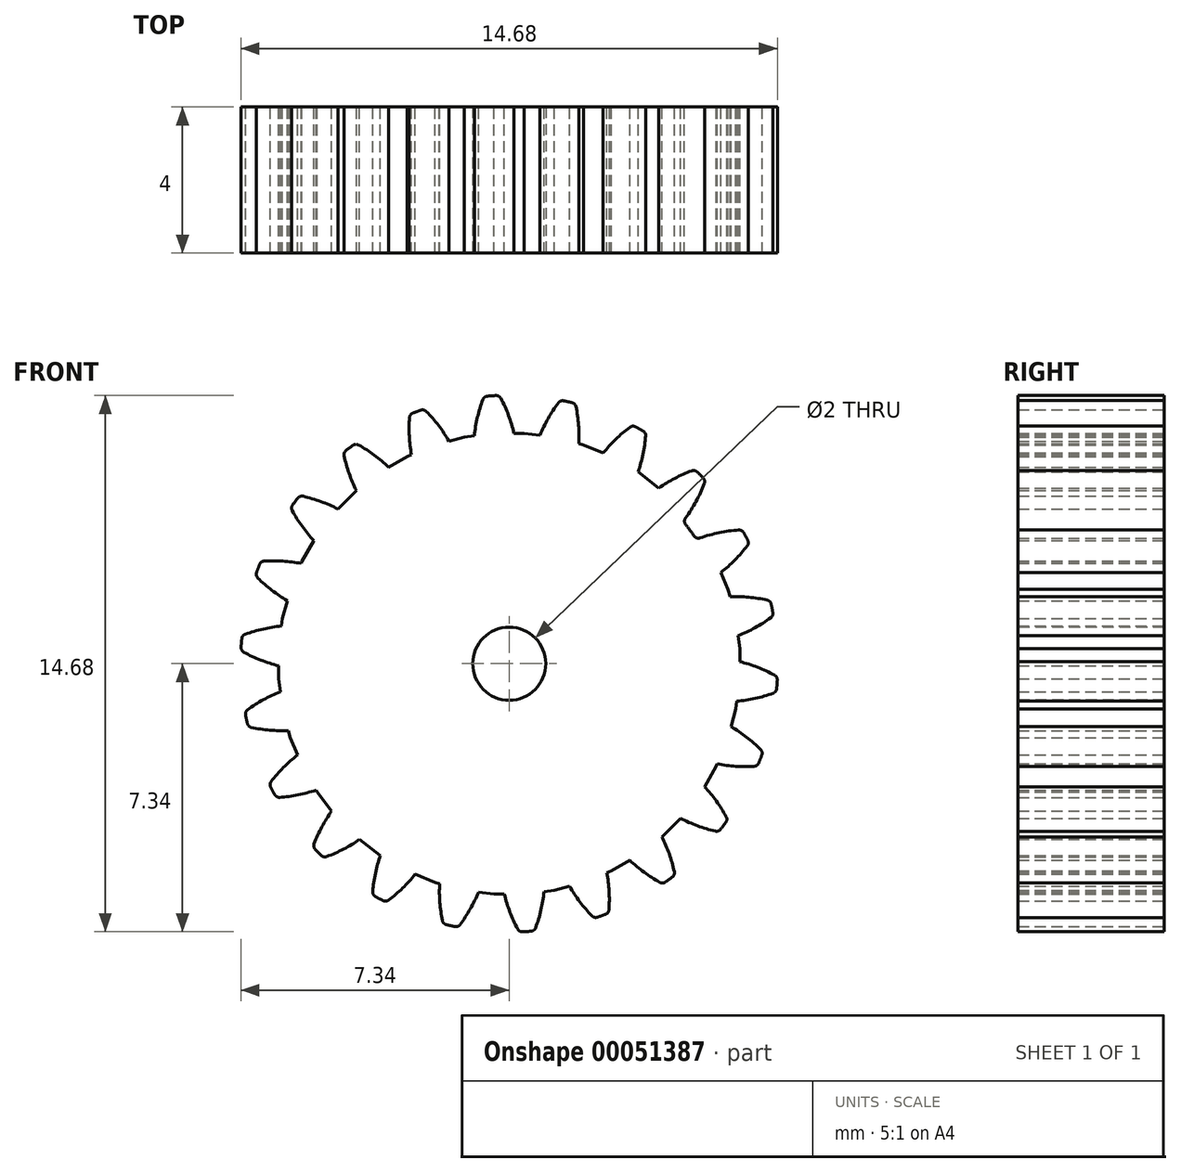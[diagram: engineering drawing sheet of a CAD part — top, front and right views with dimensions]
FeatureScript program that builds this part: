
annotation { "Feature Type Name" : "Feature", "Feature Type Description" : "" }
export const myFeature = defineFeature(function(context is Context, id is Id, definition is map)
    precondition{}
    {
        {
            var Q0;
            Q0=qCreatedBy(makeId("Front.planeOp"),FACE);
            var sketch = newSketch(context, id + "F0", { "sketchPlane" : qUnion([Q0])});
            skCircle(sketch, "E0", {"center": v(0, 0) * mm, "radius": 6.15 * mm, "construction": true});
            skCircle(sketch, "E1", {"center": v(0, 0) * mm, "radius": 6.75 * mm, "construction": true});
            skCircle(sketch, "E2", {"center": v(0, 0) * mm, "radius": 7.35 * mm, "construction": true});
            skLineSegment(sketch, "E3", {"start": v(0, 0) * mm, "end": v(0, 6.31) * mm, "construction": true});
            skCircle(sketch, "E4", {"center": v(0, 6.75) * mm, "radius": 4.05 * mm, "construction": true});
            skCircle(sketch, "E5.cCircle", {"center": v(0, 0) * mm, "radius": 6.31 * mm, "construction": true});
            skLineSegment(sketch, "E5.0", {"start": v(0, 6.31) * mm, "end": v(0.82, 6.26) * mm, "construction": true});
            skLineSegment(sketch, "E5.1", {"start": v(0.82, 6.26) * mm, "end": v(1.63, 6.1) * mm, "construction": true});
            skLineSegment(sketch, "E5.2", {"start": v(1.63, 6.1) * mm, "end": v(2.41, 5.83) * mm, "construction": true});
            skLineSegment(sketch, "E5.3", {"start": v(2.41, 5.83) * mm, "end": v(3.16, 5.46) * mm, "construction": true});
            skLineSegment(sketch, "E5.4", {"start": v(3.16, 5.46) * mm, "end": v(3.84, 5) * mm, "construction": true});
            skLineSegment(sketch, "E5.5", {"start": v(3.84, 5) * mm, "end": v(4.46, 4.46) * mm, "construction": true});
            skLineSegment(sketch, "E5.6", {"start": v(4.46, 4.46) * mm, "end": v(5, 3.84) * mm, "construction": true});
            skLineSegment(sketch, "E5.7", {"start": v(5, 3.84) * mm, "end": v(5.46, 3.16) * mm, "construction": true});
            skLineSegment(sketch, "E5.8", {"start": v(5.46, 3.16) * mm, "end": v(5.83, 2.41) * mm, "construction": true});
            skLineSegment(sketch, "E5.9", {"start": v(5.83, 2.41) * mm, "end": v(6.1, 1.63) * mm, "construction": true});
            skLineSegment(sketch, "E5.10", {"start": v(6.1, 1.63) * mm, "end": v(6.26, 0.82) * mm, "construction": true});
            skLineSegment(sketch, "E5.11", {"start": v(6.26, 0.82) * mm, "end": v(6.31, 0) * mm, "construction": true});
            skLineSegment(sketch, "E5.12", {"start": v(6.31, 0) * mm, "end": v(6.26, -0.82) * mm, "construction": true});
            skLineSegment(sketch, "E5.13", {"start": v(6.26, -0.82) * mm, "end": v(6.1, -1.63) * mm, "construction": true});
            skLineSegment(sketch, "E5.14", {"start": v(6.1, -1.63) * mm, "end": v(5.83, -2.41) * mm, "construction": true});
            skLineSegment(sketch, "E5.15", {"start": v(5.83, -2.41) * mm, "end": v(5.46, -3.16) * mm, "construction": true});
            skLineSegment(sketch, "E5.16", {"start": v(5.46, -3.16) * mm, "end": v(5, -3.84) * mm, "construction": true});
            skLineSegment(sketch, "E5.17", {"start": v(5, -3.84) * mm, "end": v(4.46, -4.46) * mm, "construction": true});
            skLineSegment(sketch, "E5.18", {"start": v(4.46, -4.46) * mm, "end": v(3.84, -5) * mm, "construction": true});
            skLineSegment(sketch, "E5.19", {"start": v(3.84, -5) * mm, "end": v(3.16, -5.46) * mm, "construction": true});
            skLineSegment(sketch, "E5.20", {"start": v(3.16, -5.46) * mm, "end": v(2.41, -5.83) * mm, "construction": true});
            skLineSegment(sketch, "E5.21", {"start": v(2.41, -5.83) * mm, "end": v(1.63, -6.1) * mm, "construction": true});
            skLineSegment(sketch, "E5.22", {"start": v(1.63, -6.1) * mm, "end": v(0.82, -6.26) * mm, "construction": true});
            skLineSegment(sketch, "E5.23", {"start": v(0.82, -6.26) * mm, "end": v(0, -6.31) * mm, "construction": true});
            skLineSegment(sketch, "E5.24", {"start": v(0, -6.31) * mm, "end": v(-0.82, -6.26) * mm, "construction": true});
            skLineSegment(sketch, "E5.25", {"start": v(-0.82, -6.26) * mm, "end": v(-1.63, -6.1) * mm, "construction": true});
            skLineSegment(sketch, "E5.26", {"start": v(-1.63, -6.1) * mm, "end": v(-2.41, -5.83) * mm, "construction": true});
            skLineSegment(sketch, "E5.27", {"start": v(-2.41, -5.83) * mm, "end": v(-3.16, -5.46) * mm, "construction": true});
            skLineSegment(sketch, "E5.28", {"start": v(-3.16, -5.46) * mm, "end": v(-3.84, -5) * mm, "construction": true});
            skLineSegment(sketch, "E5.29", {"start": v(-3.84, -5) * mm, "end": v(-4.46, -4.46) * mm, "construction": true});
            skLineSegment(sketch, "E5.30", {"start": v(-4.46, -4.46) * mm, "end": v(-5, -3.84) * mm, "construction": true});
            skLineSegment(sketch, "E5.31", {"start": v(-5, -3.84) * mm, "end": v(-5.46, -3.16) * mm, "construction": true});
            skLineSegment(sketch, "E5.32", {"start": v(-5.46, -3.16) * mm, "end": v(-5.83, -2.41) * mm, "construction": true});
            skLineSegment(sketch, "E5.33", {"start": v(-5.83, -2.41) * mm, "end": v(-6.1, -1.63) * mm, "construction": true});
            skLineSegment(sketch, "E5.34", {"start": v(-6.1, -1.63) * mm, "end": v(-6.26, -0.82) * mm, "construction": true});
            skLineSegment(sketch, "E5.35", {"start": v(-6.26, -0.82) * mm, "end": v(-6.31, 0) * mm, "construction": true});
            skLineSegment(sketch, "E5.36", {"start": v(-6.31, 0) * mm, "end": v(-6.26, 0.82) * mm, "construction": true});
            skLineSegment(sketch, "E5.37", {"start": v(-6.26, 0.82) * mm, "end": v(-6.1, 1.63) * mm, "construction": true});
            skLineSegment(sketch, "E5.38", {"start": v(-6.1, 1.63) * mm, "end": v(-5.83, 2.41) * mm, "construction": true});
            skLineSegment(sketch, "E5.39", {"start": v(-5.83, 2.41) * mm, "end": v(-5.46, 3.16) * mm, "construction": true});
            skLineSegment(sketch, "E5.40", {"start": v(-5.46, 3.16) * mm, "end": v(-5, 3.84) * mm, "construction": true});
            skLineSegment(sketch, "E5.41", {"start": v(-5, 3.84) * mm, "end": v(-4.46, 4.46) * mm, "construction": true});
            skLineSegment(sketch, "E5.42", {"start": v(-4.46, 4.46) * mm, "end": v(-3.84, 5) * mm, "construction": true});
            skLineSegment(sketch, "E5.43", {"start": v(-3.84, 5) * mm, "end": v(-3.16, 5.46) * mm, "construction": true});
            skLineSegment(sketch, "E5.44", {"start": v(-3.16, 5.46) * mm, "end": v(-2.41, 5.83) * mm, "construction": true});
            skLineSegment(sketch, "E5.45", {"start": v(-2.41, 5.83) * mm, "end": v(-1.63, 6.1) * mm, "construction": true});
            skLineSegment(sketch, "E5.46", {"start": v(-1.63, 6.1) * mm, "end": v(-0.82, 6.26) * mm, "construction": true});
            skLineSegment(sketch, "E5.47", {"start": v(-0.82, 6.26) * mm, "end": v(0, 6.31) * mm, "construction": true});
            skLineSegment(sketch, "E6.0", {"start": v(-0.41, 6.31) * mm, "end": v(0.41, 6.31) * mm});
            skLineSegment(sketch, "E6.1", {"start": v(0.41, 6.31) * mm, "end": v(1.23, 6.2) * mm});
            skLineSegment(sketch, "E6.2", {"start": v(1.23, 6.2) * mm, "end": v(2.03, 5.99) * mm});
            skLineSegment(sketch, "E6.3", {"start": v(2.03, 5.99) * mm, "end": v(2.8, 5.67) * mm});
            skLineSegment(sketch, "E6.4", {"start": v(2.8, 5.67) * mm, "end": v(3.51, 5.26) * mm});
            skLineSegment(sketch, "E6.5", {"start": v(3.51, 5.26) * mm, "end": v(4.17, 4.75) * mm});
            skLineSegment(sketch, "E6.6", {"start": v(4.17, 4.75) * mm, "end": v(4.75, 4.17) * mm});
            skLineSegment(sketch, "E6.7", {"start": v(4.75, 4.17) * mm, "end": v(5.26, 3.51) * mm, "construction": true});
            skLineSegment(sketch, "E6.8", {"start": v(5.26, 3.51) * mm, "end": v(5.67, 2.8) * mm});
            skLineSegment(sketch, "E6.9", {"start": v(5.67, 2.8) * mm, "end": v(5.99, 2.03) * mm});
            skLineSegment(sketch, "E6.10", {"start": v(5.99, 2.03) * mm, "end": v(6.2, 1.23) * mm});
            skLineSegment(sketch, "E6.11", {"start": v(6.2, 1.23) * mm, "end": v(6.31, 0.41) * mm});
            skLineSegment(sketch, "E6.12", {"start": v(6.31, 0.41) * mm, "end": v(6.31, -0.41) * mm});
            skLineSegment(sketch, "E6.13", {"start": v(6.31, -0.41) * mm, "end": v(6.2, -1.23) * mm});
            skLineSegment(sketch, "E6.14", {"start": v(6.2, -1.23) * mm, "end": v(5.99, -2.03) * mm});
            skLineSegment(sketch, "E6.15", {"start": v(5.99, -2.03) * mm, "end": v(5.67, -2.8) * mm});
            skLineSegment(sketch, "E6.16", {"start": v(5.67, -2.8) * mm, "end": v(5.26, -3.51) * mm});
            skLineSegment(sketch, "E6.17", {"start": v(5.26, -3.51) * mm, "end": v(4.75, -4.17) * mm});
            skLineSegment(sketch, "E6.18", {"start": v(4.75, -4.17) * mm, "end": v(4.17, -4.75) * mm});
            skLineSegment(sketch, "E6.19", {"start": v(4.17, -4.75) * mm, "end": v(3.51, -5.26) * mm});
            skLineSegment(sketch, "E6.20", {"start": v(3.51, -5.26) * mm, "end": v(2.8, -5.67) * mm});
            skLineSegment(sketch, "E6.21", {"start": v(2.8, -5.67) * mm, "end": v(2.03, -5.99) * mm});
            skLineSegment(sketch, "E6.22", {"start": v(2.03, -5.99) * mm, "end": v(1.23, -6.2) * mm});
            skLineSegment(sketch, "E6.23", {"start": v(1.23, -6.2) * mm, "end": v(0.41, -6.31) * mm});
            skLineSegment(sketch, "E6.24", {"start": v(0.41, -6.31) * mm, "end": v(-0.41, -6.31) * mm});
            skLineSegment(sketch, "E6.25", {"start": v(-0.41, -6.31) * mm, "end": v(-1.23, -6.2) * mm});
            skLineSegment(sketch, "E6.26", {"start": v(-1.23, -6.2) * mm, "end": v(-2.03, -5.99) * mm});
            skLineSegment(sketch, "E6.27", {"start": v(-2.03, -5.99) * mm, "end": v(-2.8, -5.67) * mm});
            skLineSegment(sketch, "E6.28", {"start": v(-2.8, -5.67) * mm, "end": v(-3.51, -5.26) * mm});
            skLineSegment(sketch, "E6.29", {"start": v(-3.51, -5.26) * mm, "end": v(-4.17, -4.75) * mm});
            skLineSegment(sketch, "E6.30", {"start": v(-4.17, -4.75) * mm, "end": v(-4.75, -4.17) * mm});
            skLineSegment(sketch, "E6.31", {"start": v(-4.75, -4.17) * mm, "end": v(-5.26, -3.51) * mm});
            skLineSegment(sketch, "E6.32", {"start": v(-5.26, -3.51) * mm, "end": v(-5.67, -2.8) * mm});
            skLineSegment(sketch, "E6.33", {"start": v(-5.67, -2.8) * mm, "end": v(-5.99, -2.03) * mm});
            skLineSegment(sketch, "E6.34", {"start": v(-5.99, -2.03) * mm, "end": v(-6.2, -1.23) * mm});
            skLineSegment(sketch, "E6.35", {"start": v(-6.2, -1.23) * mm, "end": v(-6.31, -0.41) * mm});
            skLineSegment(sketch, "E6.36", {"start": v(-6.31, -0.41) * mm, "end": v(-6.31, 0.41) * mm});
            skLineSegment(sketch, "E6.37", {"start": v(-6.31, 0.41) * mm, "end": v(-6.2, 1.23) * mm});
            skLineSegment(sketch, "E6.38", {"start": v(-6.2, 1.23) * mm, "end": v(-5.99, 2.03) * mm});
            skLineSegment(sketch, "E6.39", {"start": v(-5.99, 2.03) * mm, "end": v(-5.67, 2.8) * mm});
            skLineSegment(sketch, "E6.40", {"start": v(-5.67, 2.8) * mm, "end": v(-5.26, 3.51) * mm});
            skLineSegment(sketch, "E6.41", {"start": v(-5.26, 3.51) * mm, "end": v(-4.75, 4.17) * mm});
            skLineSegment(sketch, "E6.42", {"start": v(-4.75, 4.17) * mm, "end": v(-4.17, 4.75) * mm});
            skLineSegment(sketch, "E6.43", {"start": v(-4.17, 4.75) * mm, "end": v(-3.51, 5.26) * mm});
            skLineSegment(sketch, "E6.44", {"start": v(-3.51, 5.26) * mm, "end": v(-2.8, 5.67) * mm});
            skLineSegment(sketch, "E6.45", {"start": v(-2.8, 5.67) * mm, "end": v(-2.03, 5.99) * mm});
            skLineSegment(sketch, "E6.46", {"start": v(-2.03, 5.99) * mm, "end": v(-1.23, 6.2) * mm});
            skLineSegment(sketch, "E6.47", {"start": v(-1.23, 6.2) * mm, "end": v(-0.41, 6.31) * mm});
            skPoint(sketch, "E6.0.midPoint", {"position": v(0, 6.31) * mm});
            skLineSegment(sketch, "E7", {"start": v(0, 6.75) * mm, "end": v(-9.03, 6.75) * mm, "construction": true});
            skLineSegment(sketch, "E8", {"start": v(0, 6.75) * mm, "end": v(-8.97, 3.48) * mm, "construction": true});
            skCircle(sketch, "E9", {"center": v(-3.8, 5.36) * mm, "radius": 4.05 * mm, "construction": true});
            skArc(sketch, "E10", {"start": v(-0.23, 7.26) * mm, "mid": v(0, 6.77) * mm, "end": v(0.15, 6.26) * mm});
            skLineSegment(sketch, "E11", {"start": v(0, 0) * mm, "end": v(-0.41, 6.31) * mm, "construction": true});
            skArc(sketch, "E12.MirrorCS", {"start": v(-0.72, 7.23) * mm, "mid": v(-0.88, 6.72) * mm, "end": v(-0.96, 6.18) * mm});
            skArc(sketch, "E13", {"start": v(-0.6, 7.33) * mm, "mid": v(-0.48, 7.33) * mm, "end": v(-0.36, 7.34) * mm});
            skArc(sketch, "E14", {"start": v(-1.08, 6.05) * mm, "mid": v(0.4, -6.14) * mm, "end": v(0.28, 6.14) * mm});
            skPoint(sketch, "E15.visualSharp", {"position": v(-0.97, 6.07) * mm});
            skArc(sketch, "E15.filletArc", {"start": v(-1.08, 6.05) * mm, "mid": v(-1, 6.1) * mm, "end": v(-0.96, 6.18) * mm});
            skPoint(sketch, "E16.visualSharp", {"position": v(0.17, 6.15) * mm});
            skArc(sketch, "E16.filletArc", {"start": v(0.15, 6.26) * mm, "mid": v(0.2, 6.18) * mm, "end": v(0.28, 6.14) * mm});
            skPoint(sketch, "E17.visualSharp", {"position": v(-0.69, 7.32) * mm});
            skArc(sketch, "E17.filletArc", {"start": v(-0.6, 7.33) * mm, "mid": v(-0.67, 7.3) * mm, "end": v(-0.72, 7.23) * mm});
            skPoint(sketch, "E18.visualSharp", {"position": v(-0.27, 7.34) * mm});
            skArc(sketch, "E18.filletArc", {"start": v(-0.23, 7.26) * mm, "mid": v(-0.29, 7.32) * mm, "end": v(-0.36, 7.34) * mm});
            skArc(sketch, "E19.1.0", {"start": v(-2.74, 5.5) * mm, "mid": v(-2.68, 5.57) * mm, "end": v(-2.66, 5.66) * mm});
            skArc(sketch, "E19.1.1", {"start": v(-2.73, 6.74) * mm, "mid": v(-2.73, 6.2) * mm, "end": v(-2.66, 5.66) * mm});
            skArc(sketch, "E19.1.2", {"start": v(-2.64, 6.86) * mm, "mid": v(-2.7, 6.81) * mm, "end": v(-2.73, 6.74) * mm});
            skArc(sketch, "E19.1.3", {"start": v(-2.64, 6.86) * mm, "mid": v(-2.53, 6.9) * mm, "end": v(-2.42, 6.94) * mm});
            skArc(sketch, "E19.1.4", {"start": v(-2.27, 6.9) * mm, "mid": v(-2.34, 6.95) * mm, "end": v(-2.42, 6.94) * mm});
            skArc(sketch, "E19.1.5", {"start": v(-2.27, 6.9) * mm, "mid": v(-1.92, 6.5) * mm, "end": v(-1.62, 6.04) * mm});
            skArc(sketch, "E19.1.6", {"start": v(-1.62, 6.04) * mm, "mid": v(-1.56, 5.98) * mm, "end": v(-1.46, 5.97) * mm});
            skArc(sketch, "E19.2.0", {"start": v(-4.18, 4.51) * mm, "mid": v(-4.14, 4.6) * mm, "end": v(-4.15, 4.68) * mm});
            skArc(sketch, "E19.2.1", {"start": v(-4.52, 5.7) * mm, "mid": v(-4.37, 5.18) * mm, "end": v(-4.15, 4.68) * mm});
            skArc(sketch, "E19.2.2", {"start": v(-4.46, 5.84) * mm, "mid": v(-4.51, 5.77) * mm, "end": v(-4.52, 5.7) * mm});
            skArc(sketch, "E19.2.3", {"start": v(-4.46, 5.84) * mm, "mid": v(-4.37, 5.91) * mm, "end": v(-4.27, 5.98) * mm});
            skArc(sketch, "E19.2.4", {"start": v(-4.12, 5.99) * mm, "mid": v(-4.2, 6) * mm, "end": v(-4.27, 5.98) * mm});
            skArc(sketch, "E19.2.5", {"start": v(-4.12, 5.99) * mm, "mid": v(-3.67, 5.7) * mm, "end": v(-3.26, 5.34) * mm});
            skArc(sketch, "E19.2.6", {"start": v(-3.26, 5.34) * mm, "mid": v(-3.18, 5.3) * mm, "end": v(-3.09, 5.32) * mm});
            skArc(sketch, "E19.3.0", {"start": v(-5.28, 3.15) * mm, "mid": v(-5.26, 3.24) * mm, "end": v(-5.3, 3.32) * mm});
            skArc(sketch, "E19.3.1", {"start": v(-5.94, 4.2) * mm, "mid": v(-5.65, 3.74) * mm, "end": v(-5.3, 3.32) * mm});
            skArc(sketch, "E19.3.2", {"start": v(-5.93, 4.35) * mm, "mid": v(-5.96, 4.27) * mm, "end": v(-5.94, 4.2) * mm});
            skArc(sketch, "E19.3.3", {"start": v(-5.93, 4.35) * mm, "mid": v(-5.86, 4.44) * mm, "end": v(-5.79, 4.53) * mm});
            skArc(sketch, "E19.3.4", {"start": v(-5.64, 4.58) * mm, "mid": v(-5.72, 4.58) * mm, "end": v(-5.79, 4.53) * mm});
            skArc(sketch, "E19.3.5", {"start": v(-5.64, 4.58) * mm, "mid": v(-5.12, 4.43) * mm, "end": v(-4.63, 4.2) * mm});
            skArc(sketch, "E19.3.6", {"start": v(-4.63, 4.2) * mm, "mid": v(-4.54, 4.2) * mm, "end": v(-4.46, 4.23) * mm});
            skArc(sketch, "E19.4.0", {"start": v(-5.96, 1.53) * mm, "mid": v(-5.96, 1.63) * mm, "end": v(-6.02, 1.7) * mm});
            skArc(sketch, "E19.4.1", {"start": v(-6.88, 2.35) * mm, "mid": v(-6.47, 2) * mm, "end": v(-6.02, 1.7) * mm});
            skArc(sketch, "E19.4.2", {"start": v(-6.91, 2.5) * mm, "mid": v(-6.92, 2.42) * mm, "end": v(-6.88, 2.35) * mm});
            skArc(sketch, "E19.4.3", {"start": v(-6.91, 2.5) * mm, "mid": v(-6.87, 2.6) * mm, "end": v(-6.83, 2.72) * mm});
            skArc(sketch, "E19.4.4", {"start": v(-6.7, 2.8) * mm, "mid": v(-6.78, 2.78) * mm, "end": v(-6.83, 2.72) * mm});
            skArc(sketch, "E19.4.5", {"start": v(-6.7, 2.8) * mm, "mid": v(-6.16, 2.8) * mm, "end": v(-5.63, 2.73) * mm});
            skArc(sketch, "E19.4.6", {"start": v(-5.63, 2.73) * mm, "mid": v(-5.54, 2.74) * mm, "end": v(-5.47, 2.8) * mm});
            skArc(sketch, "E19.5.0", {"start": v(-6.15, -0.2) * mm, "mid": v(-6.18, -0.12) * mm, "end": v(-6.26, -0.07) * mm});
            skArc(sketch, "E19.5.1", {"start": v(-7.26, 0.32) * mm, "mid": v(-6.77, 0.09) * mm, "end": v(-6.26, -0.07) * mm});
            skArc(sketch, "E19.5.2", {"start": v(-7.34, 0.45) * mm, "mid": v(-7.32, 0.37) * mm, "end": v(-7.26, 0.32) * mm});
            skArc(sketch, "E19.5.3", {"start": v(-7.34, 0.45) * mm, "mid": v(-7.33, 0.57) * mm, "end": v(-7.32, 0.69) * mm});
            skArc(sketch, "E19.5.4", {"start": v(-7.22, 0.8) * mm, "mid": v(-7.29, 0.76) * mm, "end": v(-7.32, 0.69) * mm});
            skArc(sketch, "E19.5.5", {"start": v(-7.22, 0.8) * mm, "mid": v(-6.7, 0.96) * mm, "end": v(-6.17, 1.03) * mm});
            skArc(sketch, "E19.5.6", {"start": v(-6.17, 1.03) * mm, "mid": v(-6.09, 1.07) * mm, "end": v(-6.04, 1.15) * mm});
            skArc(sketch, "E19.6.0", {"start": v(-5.84, -1.93) * mm, "mid": v(-5.9, -1.86) * mm, "end": v(-5.98, -1.83) * mm});
            skArc(sketch, "E19.6.1", {"start": v(-7.06, -1.74) * mm, "mid": v(-6.52, -1.82) * mm, "end": v(-5.98, -1.83) * mm});
            skArc(sketch, "E19.6.2", {"start": v(-7.17, -1.63) * mm, "mid": v(-7.13, -1.7) * mm, "end": v(-7.06, -1.74) * mm});
            skArc(sketch, "E19.6.3", {"start": v(-7.17, -1.63) * mm, "mid": v(-7.2, -1.52) * mm, "end": v(-7.21, -1.4) * mm});
            skArc(sketch, "E19.6.4", {"start": v(-7.16, -1.26) * mm, "mid": v(-7.2, -1.32) * mm, "end": v(-7.21, -1.4) * mm});
            skArc(sketch, "E19.6.5", {"start": v(-7.16, -1.26) * mm, "mid": v(-6.7, -0.97) * mm, "end": v(-6.21, -0.75) * mm});
            skArc(sketch, "E19.6.6", {"start": v(-6.21, -0.75) * mm, "mid": v(-6.14, -0.69) * mm, "end": v(-6.12, -0.6) * mm});
            skArc(sketch, "E19.7.0", {"start": v(-5.06, -3.5) * mm, "mid": v(-5.13, -3.44) * mm, "end": v(-5.23, -3.44) * mm});
            skArc(sketch, "E19.7.1", {"start": v(-6.28, -3.66) * mm, "mid": v(-5.75, -3.59) * mm, "end": v(-5.23, -3.44) * mm});
            skArc(sketch, "E19.7.2", {"start": v(-6.42, -3.59) * mm, "mid": v(-6.36, -3.64) * mm, "end": v(-6.28, -3.66) * mm});
            skArc(sketch, "E19.7.3", {"start": v(-6.42, -3.59) * mm, "mid": v(-6.47, -3.48) * mm, "end": v(-6.53, -3.38) * mm});
            skArc(sketch, "E19.7.4", {"start": v(-6.51, -3.23) * mm, "mid": v(-6.54, -3.3) * mm, "end": v(-6.53, -3.38) * mm});
            skArc(sketch, "E19.7.5", {"start": v(-6.51, -3.23) * mm, "mid": v(-6.16, -2.82) * mm, "end": v(-5.75, -2.47) * mm});
            skArc(sketch, "E19.7.6", {"start": v(-5.75, -2.47) * mm, "mid": v(-5.7, -2.4) * mm, "end": v(-5.7, -2.3) * mm});
            skArc(sketch, "E19.8.0", {"start": v(-3.87, -4.78) * mm, "mid": v(-3.96, -4.75) * mm, "end": v(-4.04, -4.78) * mm});
            skArc(sketch, "E19.8.1", {"start": v(-5, -5.28) * mm, "mid": v(-4.5, -5.06) * mm, "end": v(-4.04, -4.78) * mm});
            skArc(sketch, "E19.8.2", {"start": v(-5.14, -5.25) * mm, "mid": v(-5.07, -5.29) * mm, "end": v(-5, -5.28) * mm});
            skArc(sketch, "E19.8.3", {"start": v(-5.14, -5.25) * mm, "mid": v(-5.23, -5.17) * mm, "end": v(-5.31, -5.08) * mm});
            skArc(sketch, "E19.8.4", {"start": v(-5.34, -4.93) * mm, "mid": v(-5.35, -5.01) * mm, "end": v(-5.31, -5.08) * mm});
            skArc(sketch, "E19.8.5", {"start": v(-5.34, -4.93) * mm, "mid": v(-5.11, -4.44) * mm, "end": v(-4.82, -3.99) * mm});
            skArc(sketch, "E19.8.6", {"start": v(-4.82, -3.99) * mm, "mid": v(-4.8, -3.9) * mm, "end": v(-4.83, -3.81) * mm});
            skArc(sketch, "E19.9.0", {"start": v(-2.37, -5.68) * mm, "mid": v(-2.46, -5.67) * mm, "end": v(-2.54, -5.72) * mm});
            skArc(sketch, "E19.9.1", {"start": v(-3.3, -6.47) * mm, "mid": v(-2.9, -6.12) * mm, "end": v(-2.54, -5.72) * mm});
            skArc(sketch, "E19.9.2", {"start": v(-3.46, -6.49) * mm, "mid": v(-3.38, -6.5) * mm, "end": v(-3.3, -6.47) * mm});
            skArc(sketch, "E19.9.3", {"start": v(-3.46, -6.49) * mm, "mid": v(-3.56, -6.43) * mm, "end": v(-3.66, -6.37) * mm});
            skArc(sketch, "E19.9.4", {"start": v(-3.73, -6.24) * mm, "mid": v(-3.72, -6.31) * mm, "end": v(-3.66, -6.37) * mm});
            skArc(sketch, "E19.9.5", {"start": v(-3.73, -6.24) * mm, "mid": v(-3.65, -5.7) * mm, "end": v(-3.5, -5.18) * mm});
            skArc(sketch, "E19.9.6", {"start": v(-3.5, -5.18) * mm, "mid": v(-3.5, -5.1) * mm, "end": v(-3.56, -5.02) * mm});
            skArc(sketch, "E19.10.0", {"start": v(-0.67, -6.11) * mm, "mid": v(-0.76, -6.13) * mm, "end": v(-0.82, -6.2) * mm});
            skArc(sketch, "E19.10.1", {"start": v(-1.35, -7.14) * mm, "mid": v(-1.05, -6.7) * mm, "end": v(-0.82, -6.2) * mm});
            skArc(sketch, "E19.10.2", {"start": v(-1.5, -7.2) * mm, "mid": v(-1.4, -7.2) * mm, "end": v(-1.35, -7.14) * mm});
            skArc(sketch, "E19.10.3", {"start": v(-1.5, -7.2) * mm, "mid": v(-1.6, -7.17) * mm, "end": v(-1.72, -7.15) * mm});
            skArc(sketch, "E19.10.4", {"start": v(-1.83, -7.04) * mm, "mid": v(-1.79, -7.1) * mm, "end": v(-1.72, -7.15) * mm});
            skArc(sketch, "E19.10.5", {"start": v(-1.83, -7.04) * mm, "mid": v(-1.9, -6.5) * mm, "end": v(-1.9, -5.96) * mm});
            skArc(sketch, "E19.10.6", {"start": v(-1.9, -5.96) * mm, "mid": v(-1.93, -5.87) * mm, "end": v(-2, -5.82) * mm});
            skArc(sketch, "E19.11.0", {"start": v(1.08, -6.05) * mm, "mid": v(1, -6.1) * mm, "end": v(0.96, -6.18) * mm});
            skArc(sketch, "E19.11.1", {"start": v(0.72, -7.23) * mm, "mid": v(0.88, -6.72) * mm, "end": v(0.96, -6.18) * mm});
            skArc(sketch, "E19.11.2", {"start": v(0.6, -7.33) * mm, "mid": v(0.67, -7.3) * mm, "end": v(0.72, -7.23) * mm});
            skArc(sketch, "E19.11.3", {"start": v(0.6, -7.33) * mm, "mid": v(0.48, -7.33) * mm, "end": v(0.36, -7.34) * mm});
            skArc(sketch, "E19.11.4", {"start": v(0.23, -7.26) * mm, "mid": v(0.29, -7.32) * mm, "end": v(0.36, -7.34) * mm});
            skArc(sketch, "E19.11.5", {"start": v(0.23, -7.26) * mm, "mid": v(0, -6.77) * mm, "end": v(-0.15, -6.26) * mm});
            skArc(sketch, "E19.11.6", {"start": v(-0.15, -6.26) * mm, "mid": v(-0.2, -6.18) * mm, "end": v(-0.28, -6.14) * mm});
            skArc(sketch, "E19.12.0", {"start": v(2.74, -5.5) * mm, "mid": v(2.68, -5.57) * mm, "end": v(2.66, -5.66) * mm});
            skArc(sketch, "E19.12.1", {"start": v(2.73, -6.74) * mm, "mid": v(2.73, -6.2) * mm, "end": v(2.66, -5.66) * mm});
            skArc(sketch, "E19.12.2", {"start": v(2.64, -6.86) * mm, "mid": v(2.7, -6.81) * mm, "end": v(2.73, -6.74) * mm});
            skArc(sketch, "E19.12.3", {"start": v(2.64, -6.86) * mm, "mid": v(2.53, -6.9) * mm, "end": v(2.42, -6.94) * mm});
            skArc(sketch, "E19.12.4", {"start": v(2.27, -6.9) * mm, "mid": v(2.34, -6.95) * mm, "end": v(2.42, -6.94) * mm});
            skArc(sketch, "E19.12.5", {"start": v(2.27, -6.9) * mm, "mid": v(1.92, -6.5) * mm, "end": v(1.62, -6.04) * mm});
            skArc(sketch, "E19.12.6", {"start": v(1.62, -6.04) * mm, "mid": v(1.56, -5.98) * mm, "end": v(1.46, -5.97) * mm});
            skArc(sketch, "E19.13.0", {"start": v(4.18, -4.51) * mm, "mid": v(4.14, -4.6) * mm, "end": v(4.15, -4.68) * mm});
            skArc(sketch, "E19.13.1", {"start": v(4.52, -5.7) * mm, "mid": v(4.37, -5.18) * mm, "end": v(4.15, -4.68) * mm});
            skArc(sketch, "E19.13.2", {"start": v(4.46, -5.84) * mm, "mid": v(4.51, -5.77) * mm, "end": v(4.52, -5.7) * mm});
            skArc(sketch, "E19.13.3", {"start": v(4.46, -5.84) * mm, "mid": v(4.37, -5.91) * mm, "end": v(4.27, -5.98) * mm});
            skArc(sketch, "E19.13.4", {"start": v(4.12, -5.99) * mm, "mid": v(4.2, -6) * mm, "end": v(4.27, -5.98) * mm});
            skArc(sketch, "E19.13.5", {"start": v(4.12, -5.99) * mm, "mid": v(3.67, -5.7) * mm, "end": v(3.26, -5.34) * mm});
            skArc(sketch, "E19.13.6", {"start": v(3.26, -5.34) * mm, "mid": v(3.18, -5.3) * mm, "end": v(3.09, -5.32) * mm});
            skArc(sketch, "E19.14.0", {"start": v(5.28, -3.15) * mm, "mid": v(5.26, -3.24) * mm, "end": v(5.3, -3.32) * mm});
            skArc(sketch, "E19.14.1", {"start": v(5.94, -4.2) * mm, "mid": v(5.65, -3.74) * mm, "end": v(5.3, -3.32) * mm});
            skArc(sketch, "E19.14.2", {"start": v(5.93, -4.35) * mm, "mid": v(5.96, -4.27) * mm, "end": v(5.94, -4.2) * mm});
            skArc(sketch, "E19.14.3", {"start": v(5.93, -4.35) * mm, "mid": v(5.86, -4.44) * mm, "end": v(5.79, -4.53) * mm});
            skArc(sketch, "E19.14.4", {"start": v(5.64, -4.58) * mm, "mid": v(5.72, -4.58) * mm, "end": v(5.79, -4.53) * mm});
            skArc(sketch, "E19.14.5", {"start": v(5.64, -4.58) * mm, "mid": v(5.12, -4.43) * mm, "end": v(4.63, -4.2) * mm});
            skArc(sketch, "E19.14.6", {"start": v(4.63, -4.2) * mm, "mid": v(4.54, -4.2) * mm, "end": v(4.46, -4.23) * mm});
            skArc(sketch, "E19.15.0", {"start": v(5.96, -1.53) * mm, "mid": v(5.96, -1.63) * mm, "end": v(6.02, -1.7) * mm});
            skArc(sketch, "E19.15.1", {"start": v(6.88, -2.35) * mm, "mid": v(6.47, -2) * mm, "end": v(6.02, -1.7) * mm});
            skArc(sketch, "E19.15.2", {"start": v(6.91, -2.5) * mm, "mid": v(6.92, -2.42) * mm, "end": v(6.88, -2.35) * mm});
            skArc(sketch, "E19.15.3", {"start": v(6.91, -2.5) * mm, "mid": v(6.87, -2.6) * mm, "end": v(6.83, -2.72) * mm});
            skArc(sketch, "E19.15.4", {"start": v(6.7, -2.8) * mm, "mid": v(6.78, -2.78) * mm, "end": v(6.83, -2.72) * mm});
            skArc(sketch, "E19.15.5", {"start": v(6.7, -2.8) * mm, "mid": v(6.16, -2.8) * mm, "end": v(5.63, -2.73) * mm});
            skArc(sketch, "E19.15.6", {"start": v(5.63, -2.73) * mm, "mid": v(5.54, -2.74) * mm, "end": v(5.47, -2.8) * mm});
            skArc(sketch, "E19.16.0", {"start": v(6.15, 0.2) * mm, "mid": v(6.18, 0.12) * mm, "end": v(6.26, 0.07) * mm});
            skArc(sketch, "E19.16.1", {"start": v(7.26, -0.32) * mm, "mid": v(6.77, -0.09) * mm, "end": v(6.26, 0.07) * mm});
            skArc(sketch, "E19.16.2", {"start": v(7.34, -0.45) * mm, "mid": v(7.32, -0.37) * mm, "end": v(7.26, -0.32) * mm});
            skArc(sketch, "E19.16.3", {"start": v(7.34, -0.45) * mm, "mid": v(7.33, -0.57) * mm, "end": v(7.32, -0.69) * mm});
            skArc(sketch, "E19.16.4", {"start": v(7.22, -0.8) * mm, "mid": v(7.29, -0.76) * mm, "end": v(7.32, -0.69) * mm});
            skArc(sketch, "E19.16.5", {"start": v(7.22, -0.8) * mm, "mid": v(6.7, -0.96) * mm, "end": v(6.17, -1.03) * mm});
            skArc(sketch, "E19.16.6", {"start": v(6.17, -1.03) * mm, "mid": v(6.09, -1.07) * mm, "end": v(6.04, -1.15) * mm});
            skArc(sketch, "E19.17.0", {"start": v(5.84, 1.93) * mm, "mid": v(5.9, 1.86) * mm, "end": v(5.98, 1.83) * mm});
            skArc(sketch, "E19.17.1", {"start": v(7.06, 1.74) * mm, "mid": v(6.52, 1.82) * mm, "end": v(5.98, 1.83) * mm});
            skArc(sketch, "E19.17.2", {"start": v(7.17, 1.63) * mm, "mid": v(7.13, 1.7) * mm, "end": v(7.06, 1.74) * mm});
            skArc(sketch, "E19.17.3", {"start": v(7.17, 1.63) * mm, "mid": v(7.2, 1.52) * mm, "end": v(7.21, 1.4) * mm});
            skArc(sketch, "E19.17.4", {"start": v(7.16, 1.26) * mm, "mid": v(7.2, 1.32) * mm, "end": v(7.21, 1.4) * mm});
            skArc(sketch, "E19.17.5", {"start": v(7.16, 1.26) * mm, "mid": v(6.7, 0.97) * mm, "end": v(6.21, 0.75) * mm});
            skArc(sketch, "E19.17.6", {"start": v(6.21, 0.75) * mm, "mid": v(6.14, 0.69) * mm, "end": v(6.12, 0.6) * mm});
            skArc(sketch, "E19.18.0", {"start": v(5.06, 3.5) * mm, "mid": v(5.13, 3.44) * mm, "end": v(5.23, 3.44) * mm});
            skArc(sketch, "E19.18.1", {"start": v(6.28, 3.66) * mm, "mid": v(5.75, 3.59) * mm, "end": v(5.23, 3.44) * mm});
            skArc(sketch, "E19.18.2", {"start": v(6.42, 3.59) * mm, "mid": v(6.36, 3.64) * mm, "end": v(6.28, 3.66) * mm});
            skArc(sketch, "E19.18.3", {"start": v(6.42, 3.59) * mm, "mid": v(6.47, 3.48) * mm, "end": v(6.53, 3.38) * mm});
            skArc(sketch, "E19.18.4", {"start": v(6.51, 3.23) * mm, "mid": v(6.54, 3.3) * mm, "end": v(6.53, 3.38) * mm});
            skArc(sketch, "E19.18.5", {"start": v(6.51, 3.23) * mm, "mid": v(6.16, 2.82) * mm, "end": v(5.75, 2.47) * mm});
            skArc(sketch, "E19.18.6", {"start": v(5.75, 2.47) * mm, "mid": v(5.7, 2.4) * mm, "end": v(5.7, 2.3) * mm});
            skArc(sketch, "E19.19.0", {"start": v(3.87, 4.78) * mm, "mid": v(3.96, 4.75) * mm, "end": v(4.04, 4.78) * mm});
            skArc(sketch, "E19.19.1", {"start": v(5, 5.28) * mm, "mid": v(4.5, 5.06) * mm, "end": v(4.04, 4.78) * mm});
            skArc(sketch, "E19.19.2", {"start": v(5.14, 5.25) * mm, "mid": v(5.07, 5.29) * mm, "end": v(5, 5.28) * mm});
            skArc(sketch, "E19.19.3", {"start": v(5.14, 5.25) * mm, "mid": v(5.23, 5.17) * mm, "end": v(5.31, 5.08) * mm});
            skArc(sketch, "E19.19.4", {"start": v(5.34, 4.93) * mm, "mid": v(5.35, 5.01) * mm, "end": v(5.31, 5.08) * mm});
            skArc(sketch, "E19.19.5", {"start": v(5.34, 4.93) * mm, "mid": v(5.11, 4.44) * mm, "end": v(4.82, 3.99) * mm});
            skArc(sketch, "E19.19.6", {"start": v(4.82, 3.99) * mm, "mid": v(4.8, 3.9) * mm, "end": v(4.83, 3.81) * mm});
            skArc(sketch, "E19.20.0", {"start": v(2.37, 5.68) * mm, "mid": v(2.46, 5.67) * mm, "end": v(2.54, 5.72) * mm});
            skArc(sketch, "E19.20.1", {"start": v(3.3, 6.47) * mm, "mid": v(2.9, 6.12) * mm, "end": v(2.54, 5.72) * mm});
            skArc(sketch, "E19.20.2", {"start": v(3.46, 6.49) * mm, "mid": v(3.38, 6.5) * mm, "end": v(3.3, 6.47) * mm});
            skArc(sketch, "E19.20.3", {"start": v(3.46, 6.49) * mm, "mid": v(3.56, 6.43) * mm, "end": v(3.66, 6.37) * mm});
            skArc(sketch, "E19.20.4", {"start": v(3.73, 6.24) * mm, "mid": v(3.72, 6.31) * mm, "end": v(3.66, 6.37) * mm});
            skArc(sketch, "E19.20.5", {"start": v(3.73, 6.24) * mm, "mid": v(3.65, 5.7) * mm, "end": v(3.5, 5.18) * mm});
            skArc(sketch, "E19.20.6", {"start": v(3.5, 5.18) * mm, "mid": v(3.5, 5.1) * mm, "end": v(3.56, 5.02) * mm});
            skArc(sketch, "E19.21.0", {"start": v(0.67, 6.11) * mm, "mid": v(0.76, 6.13) * mm, "end": v(0.82, 6.2) * mm});
            skArc(sketch, "E19.21.1", {"start": v(1.35, 7.14) * mm, "mid": v(1.05, 6.7) * mm, "end": v(0.82, 6.2) * mm});
            skArc(sketch, "E19.21.2", {"start": v(1.5, 7.2) * mm, "mid": v(1.4, 7.2) * mm, "end": v(1.35, 7.14) * mm});
            skArc(sketch, "E19.21.3", {"start": v(1.5, 7.2) * mm, "mid": v(1.6, 7.17) * mm, "end": v(1.72, 7.15) * mm});
            skArc(sketch, "E19.21.4", {"start": v(1.83, 7.04) * mm, "mid": v(1.79, 7.1) * mm, "end": v(1.72, 7.15) * mm});
            skArc(sketch, "E19.21.5", {"start": v(1.83, 7.04) * mm, "mid": v(1.9, 6.5) * mm, "end": v(1.9, 5.96) * mm});
            skArc(sketch, "E19.21.6", {"start": v(1.9, 5.96) * mm, "mid": v(1.93, 5.87) * mm, "end": v(2, 5.82) * mm});
            skSolve(sketch);
        }
        {
            var Q0;
            Q0=qSketchRegion(id+"F0",true);
            extrude(context, id + "F1", {"entities" : qUnion([Q0]), "depth" : 4 * mm});
        }
        {
            var Q0;
            Q0=makeQuery(id+"F1.opExtrude","CAP_FACE",FACE,{"disambiguationData":[OSD([sQuery(id+"F0.wireOp",EDGE,"E10"),sQuery(id+"F0.wireOp",EDGE,"E12.MirrorCS"),sQuery(id+"F0.wireOp",EDGE,"E13"),sQuery(id+"F0.wireOp",EDGE,"E14"),sQuery(id+"F0.wireOp",EDGE,"E15.filletArc"),sQuery(id+"F0.wireOp",EDGE,"E16.filletArc"),sQuery(id+"F0.wireOp",EDGE,"E17.filletArc"),sQuery(id+"F0.wireOp",EDGE,"E18.filletArc"),sQuery(id+"F0.wireOp",EDGE,"E19.1.0"),sQuery(id+"F0.wireOp",EDGE,"E19.1.1"),sQuery(id+"F0.wireOp",EDGE,"E19.1.2"),sQuery(id+"F0.wireOp",EDGE,"E19.1.3"),sQuery(id+"F0.wireOp",EDGE,"E19.1.4"),sQuery(id+"F0.wireOp",EDGE,"E19.1.5"),sQuery(id+"F0.wireOp",EDGE,"E19.1.6"),sQuery(id+"F0.wireOp",EDGE,"E19.2.0"),sQuery(id+"F0.wireOp",EDGE,"E19.2.1"),sQuery(id+"F0.wireOp",EDGE,"E19.2.2"),sQuery(id+"F0.wireOp",EDGE,"E19.2.3"),sQuery(id+"F0.wireOp",EDGE,"E19.2.4"),sQuery(id+"F0.wireOp",EDGE,"E19.2.5"),sQuery(id+"F0.wireOp",EDGE,"E19.2.6"),sQuery(id+"F0.wireOp",EDGE,"E19.3.0"),sQuery(id+"F0.wireOp",EDGE,"E19.3.1"),sQuery(id+"F0.wireOp",EDGE,"E19.3.2"),sQuery(id+"F0.wireOp",EDGE,"E19.3.3"),sQuery(id+"F0.wireOp",EDGE,"E19.3.4"),sQuery(id+"F0.wireOp",EDGE,"E19.3.5"),sQuery(id+"F0.wireOp",EDGE,"E19.3.6"),sQuery(id+"F0.wireOp",EDGE,"E19.4.0"),sQuery(id+"F0.wireOp",EDGE,"E19.4.1"),sQuery(id+"F0.wireOp",EDGE,"E19.4.2"),sQuery(id+"F0.wireOp",EDGE,"E19.4.3"),sQuery(id+"F0.wireOp",EDGE,"E19.4.4"),sQuery(id+"F0.wireOp",EDGE,"E19.4.5"),sQuery(id+"F0.wireOp",EDGE,"E19.4.6"),sQuery(id+"F0.wireOp",EDGE,"E19.5.0"),sQuery(id+"F0.wireOp",EDGE,"E19.5.1"),sQuery(id+"F0.wireOp",EDGE,"E19.5.2"),sQuery(id+"F0.wireOp",EDGE,"E19.5.3"),sQuery(id+"F0.wireOp",EDGE,"E19.5.4"),sQuery(id+"F0.wireOp",EDGE,"E19.5.5"),sQuery(id+"F0.wireOp",EDGE,"E19.5.6"),sQuery(id+"F0.wireOp",EDGE,"E19.6.0"),sQuery(id+"F0.wireOp",EDGE,"E19.6.1"),sQuery(id+"F0.wireOp",EDGE,"E19.6.2"),sQuery(id+"F0.wireOp",EDGE,"E19.6.3"),sQuery(id+"F0.wireOp",EDGE,"E19.6.4"),sQuery(id+"F0.wireOp",EDGE,"E19.6.5"),sQuery(id+"F0.wireOp",EDGE,"E19.6.6"),sQuery(id+"F0.wireOp",EDGE,"E19.7.0"),sQuery(id+"F0.wireOp",EDGE,"E19.7.1"),sQuery(id+"F0.wireOp",EDGE,"E19.7.2"),sQuery(id+"F0.wireOp",EDGE,"E19.7.3"),sQuery(id+"F0.wireOp",EDGE,"E19.7.4"),sQuery(id+"F0.wireOp",EDGE,"E19.7.5"),sQuery(id+"F0.wireOp",EDGE,"E19.7.6"),sQuery(id+"F0.wireOp",EDGE,"E19.8.0"),sQuery(id+"F0.wireOp",EDGE,"E19.8.1"),sQuery(id+"F0.wireOp",EDGE,"E19.8.2"),sQuery(id+"F0.wireOp",EDGE,"E19.8.3"),sQuery(id+"F0.wireOp",EDGE,"E19.8.4"),sQuery(id+"F0.wireOp",EDGE,"E19.8.5"),sQuery(id+"F0.wireOp",EDGE,"E19.8.6"),sQuery(id+"F0.wireOp",EDGE,"E19.9.0"),sQuery(id+"F0.wireOp",EDGE,"E19.9.1"),sQuery(id+"F0.wireOp",EDGE,"E19.9.2"),sQuery(id+"F0.wireOp",EDGE,"E19.9.3"),sQuery(id+"F0.wireOp",EDGE,"E19.9.4"),sQuery(id+"F0.wireOp",EDGE,"E19.9.5"),sQuery(id+"F0.wireOp",EDGE,"E19.9.6"),sQuery(id+"F0.wireOp",EDGE,"E19.10.0"),sQuery(id+"F0.wireOp",EDGE,"E19.10.1"),sQuery(id+"F0.wireOp",EDGE,"E19.10.2"),sQuery(id+"F0.wireOp",EDGE,"E19.10.3"),sQuery(id+"F0.wireOp",EDGE,"E19.10.4"),sQuery(id+"F0.wireOp",EDGE,"E19.10.5"),sQuery(id+"F0.wireOp",EDGE,"E19.10.6"),sQuery(id+"F0.wireOp",EDGE,"E19.11.0"),sQuery(id+"F0.wireOp",EDGE,"E19.11.1"),sQuery(id+"F0.wireOp",EDGE,"E19.11.2"),sQuery(id+"F0.wireOp",EDGE,"E19.11.3"),sQuery(id+"F0.wireOp",EDGE,"E19.11.4"),sQuery(id+"F0.wireOp",EDGE,"E19.11.5"),sQuery(id+"F0.wireOp",EDGE,"E19.11.6"),sQuery(id+"F0.wireOp",EDGE,"E19.12.0"),sQuery(id+"F0.wireOp",EDGE,"E19.12.1"),sQuery(id+"F0.wireOp",EDGE,"E19.12.2"),sQuery(id+"F0.wireOp",EDGE,"E19.12.3"),sQuery(id+"F0.wireOp",EDGE,"E19.12.4"),sQuery(id+"F0.wireOp",EDGE,"E19.12.5"),sQuery(id+"F0.wireOp",EDGE,"E19.12.6"),sQuery(id+"F0.wireOp",EDGE,"E19.13.0"),sQuery(id+"F0.wireOp",EDGE,"E19.13.1"),sQuery(id+"F0.wireOp",EDGE,"E19.13.2"),sQuery(id+"F0.wireOp",EDGE,"E19.13.3"),sQuery(id+"F0.wireOp",EDGE,"E19.13.4"),sQuery(id+"F0.wireOp",EDGE,"E19.13.5"),sQuery(id+"F0.wireOp",EDGE,"E19.13.6"),sQuery(id+"F0.wireOp",EDGE,"E19.14.0"),sQuery(id+"F0.wireOp",EDGE,"E19.14.1"),sQuery(id+"F0.wireOp",EDGE,"E19.14.2"),sQuery(id+"F0.wireOp",EDGE,"E19.14.3"),sQuery(id+"F0.wireOp",EDGE,"E19.14.4"),sQuery(id+"F0.wireOp",EDGE,"E19.14.5"),sQuery(id+"F0.wireOp",EDGE,"E19.14.6"),sQuery(id+"F0.wireOp",EDGE,"E19.15.0"),sQuery(id+"F0.wireOp",EDGE,"E19.15.1"),sQuery(id+"F0.wireOp",EDGE,"E19.15.2"),sQuery(id+"F0.wireOp",EDGE,"E19.15.3"),sQuery(id+"F0.wireOp",EDGE,"E19.15.4"),sQuery(id+"F0.wireOp",EDGE,"E19.15.5"),sQuery(id+"F0.wireOp",EDGE,"E19.15.6"),sQuery(id+"F0.wireOp",EDGE,"E19.16.0"),sQuery(id+"F0.wireOp",EDGE,"E19.16.1"),sQuery(id+"F0.wireOp",EDGE,"E19.16.2"),sQuery(id+"F0.wireOp",EDGE,"E19.16.3"),sQuery(id+"F0.wireOp",EDGE,"E19.16.4"),sQuery(id+"F0.wireOp",EDGE,"E19.16.5"),sQuery(id+"F0.wireOp",EDGE,"E19.16.6"),sQuery(id+"F0.wireOp",EDGE,"E19.17.0"),sQuery(id+"F0.wireOp",EDGE,"E19.17.1"),sQuery(id+"F0.wireOp",EDGE,"E19.17.2"),sQuery(id+"F0.wireOp",EDGE,"E19.17.3"),sQuery(id+"F0.wireOp",EDGE,"E19.17.4"),sQuery(id+"F0.wireOp",EDGE,"E19.17.5"),sQuery(id+"F0.wireOp",EDGE,"E19.17.6"),sQuery(id+"F0.wireOp",EDGE,"E19.18.0"),sQuery(id+"F0.wireOp",EDGE,"E19.18.1"),sQuery(id+"F0.wireOp",EDGE,"E19.18.2"),sQuery(id+"F0.wireOp",EDGE,"E19.18.3"),sQuery(id+"F0.wireOp",EDGE,"E19.18.4"),sQuery(id+"F0.wireOp",EDGE,"E19.18.5"),sQuery(id+"F0.wireOp",EDGE,"E19.18.6"),sQuery(id+"F0.wireOp",EDGE,"E19.19.0"),sQuery(id+"F0.wireOp",EDGE,"E19.19.1"),sQuery(id+"F0.wireOp",EDGE,"E19.19.2"),sQuery(id+"F0.wireOp",EDGE,"E19.19.3"),sQuery(id+"F0.wireOp",EDGE,"E19.19.4"),sQuery(id+"F0.wireOp",EDGE,"E19.19.5"),sQuery(id+"F0.wireOp",EDGE,"E19.19.6"),sQuery(id+"F0.wireOp",EDGE,"E19.20.0"),sQuery(id+"F0.wireOp",EDGE,"E19.20.1"),sQuery(id+"F0.wireOp",EDGE,"E19.20.2"),sQuery(id+"F0.wireOp",EDGE,"E19.20.3"),sQuery(id+"F0.wireOp",EDGE,"E19.20.4"),sQuery(id+"F0.wireOp",EDGE,"E19.20.5"),sQuery(id+"F0.wireOp",EDGE,"E19.20.6"),sQuery(id+"F0.wireOp",EDGE,"E19.21.0"),sQuery(id+"F0.wireOp",EDGE,"E19.21.1"),sQuery(id+"F0.wireOp",EDGE,"E19.21.2"),sQuery(id+"F0.wireOp",EDGE,"E19.21.3"),sQuery(id+"F0.wireOp",EDGE,"E19.21.4"),sQuery(id+"F0.wireOp",EDGE,"E19.21.5"),sQuery(id+"F0.wireOp",EDGE,"E19.21.6"),sQuery(id+"F0.wireOp",EDGE,"E19.22.0"),sQuery(id+"F0.wireOp",EDGE,"E19.22.1"),sQuery(id+"F0.wireOp",EDGE,"E19.22.2"),sQuery(id+"F0.wireOp",EDGE,"E19.22.3"),sQuery(id+"F0.wireOp",EDGE,"E19.22.4"),sQuery(id+"F0.wireOp",EDGE,"E19.22.5"),sQuery(id+"F0.wireOp",EDGE,"E19.22.6"),sQuery(id+"F0.wireOp",EDGE,"E19.23.0"),sQuery(id+"F0.wireOp",EDGE,"E19.23.1"),sQuery(id+"F0.wireOp",EDGE,"E19.23.2"),sQuery(id+"F0.wireOp",EDGE,"E19.23.3"),sQuery(id+"F0.wireOp",EDGE,"E19.23.4"),sQuery(id+"F0.wireOp",EDGE,"E19.23.5"),sQuery(id+"F0.wireOp",EDGE,"E19.23.6")])],"isStart":false});
            var sketch = newSketch(context, id + "F2", { "sketchPlane" : qUnion([Q0])});
            skCircle(sketch, "E20", {"center": v(0, 0) * mm, "radius": 1 * mm});
            skSolve(sketch);
        }
        {
            var Q0;
            Q0=qSketchRegion(id+"F2",true);
            extrude(context, id + "F3", {"entities" : qUnion([Q0]), "operationType" : NewBodyOperationType.REMOVE, "oppositeDirection" : true, "depth" : 25 * mm});
        }
    });
